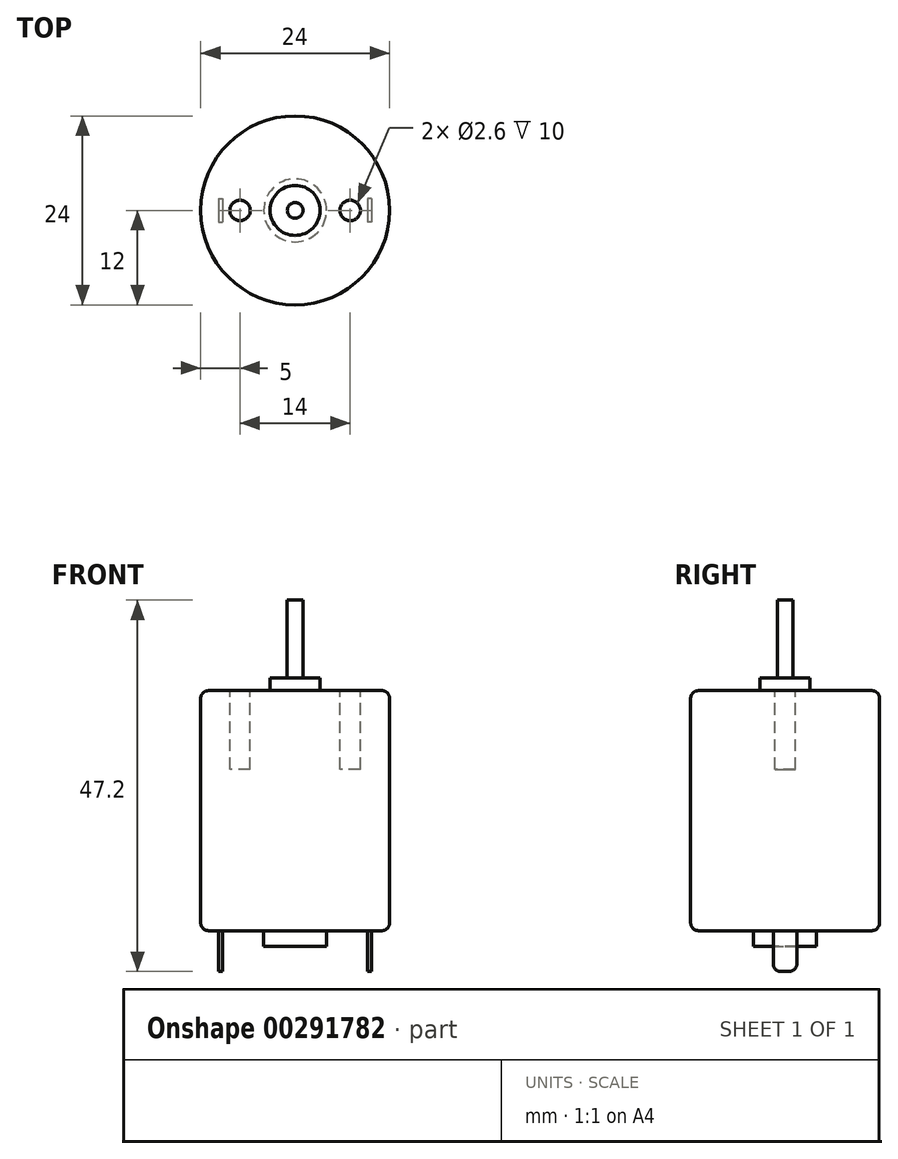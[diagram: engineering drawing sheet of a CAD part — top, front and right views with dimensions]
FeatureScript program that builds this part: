
annotation { "Feature Type Name" : "Feature", "Feature Type Description" : "" }
export const myFeature = defineFeature(function(context is Context, id is Id, definition is map)
    precondition{}
    {
        {
            var Q0;
            Q0=qCreatedBy(makeId("Top.planeOp"),FACE);
            var sketch = newSketch(context, id + "F0", { "sketchPlane" : qUnion([Q0])});
            skCircle(sketch, "E0", {"center": v(0, 0) * mm, "radius": 12 * mm});
            skSolve(sketch);
        }
        {
            var Q0;
            Q0=makeQuery(id+"F0.imprint","IMPRINT",FACE,{"disambiguationData":[TD([[makeQuery(id+"F0.imprint","IMPRINT",EDGE,{"derivedFrom":sQuery(id+"F0.wireOp",EDGE,"E0")}),1.0]])]});
            extrude(context, id + "F1", {"entities" : qUnion([Q0]), "depth" : 30.5 * mm});
        }
        {
            var Q0;
            Q0=makeQuery(id+"F1.opExtrude","CAP_FACE",FACE,{"disambiguationData":[OSD([sQuery(id+"F0.wireOp",EDGE,"E0")])],"isStart":false});
            var sketch = newSketch(context, id + "F2", { "sketchPlane" : qUnion([Q0])});
            skCircle(sketch, "E1", {"center": v(0, 0) * mm, "radius": 1 * mm});
            skSolve(sketch);
        }
        {
            var Q0;
            Q0 = qSketchRegion(id + "F2", true);
            extrude(context, id + "F3", {"entities" : qUnion([Q0]), "operationType" : NewBodyOperationType.ADD, "depth" : 11.5 * mm});
        }
        {
            var Q0;
            Q0=makeQuery(id+"F1.opExtrude","CAP_FACE",FACE,{"disambiguationData":[OSD([sQuery(id+"F0.wireOp",EDGE,"E0")])],"isStart":false});
            var sketch = newSketch(context, id + "F4", { "sketchPlane" : qUnion([Q0])});
            skCircle(sketch, "E2", {"center": v(0, 0) * mm, "radius": 3.17 * mm});
            skSolve(sketch);
        }
        {
            var Q0;
            Q0 = qSketchRegion(id + "F4", true);
            extrude(context, id + "F5", {"entities" : qUnion([Q0]), "operationType" : NewBodyOperationType.ADD, "depth" : 1.6 * mm});
        }
        {
            var Q0;
            Q0=makeQuery(id+"F1.opExtrude","CAP_FACE",FACE,{"disambiguationData":[OSD([sQuery(id+"F0.wireOp",EDGE,"E0")])],"isStart":false});
            var sketch = newSketch(context, id + "F6", { "sketchPlane" : qUnion([Q0])});
            skLineSegment(sketch, "E3", {"start": v(-12, 0) * mm, "end": v(12, 0) * mm, "construction": true});
            skCircle(sketch, "E4", {"center": v(7, 0) * mm, "radius": 1.3 * mm});
            skCircle(sketch, "E5", {"center": v(-7, 0) * mm, "radius": 1.3 * mm});
            skLineSegment(sketch, "E6", {"start": v(0, -12) * mm, "end": v(0, 12) * mm, "construction": true});
            skSolve(sketch);
        }
        {
            var Q0;
            Q0=makeQuery(id+"F6.imprint","IMPRINT",FACE,{"disambiguationData":[TD([[makeQuery(id+"F6.imprint","IMPRINT",EDGE,{"derivedFrom":sQuery(id+"F6.wireOp",EDGE,"E5")}),1.0]])]});
            var Q1;
            Q1=makeQuery(id+"F6.imprint","IMPRINT",FACE,{"disambiguationData":[TD([[makeQuery(id+"F6.imprint","IMPRINT",EDGE,{"derivedFrom":sQuery(id+"F6.wireOp",EDGE,"E4")}),1.0]])]});
            extrude(context, id + "F7", {"entities" : qUnion([Q0, Q1]), "operationType" : NewBodyOperationType.REMOVE, "oppositeDirection" : true, "depth" : 10 * mm});
        }
        {
            var Q0;
            Q0=makeQuery(id+"F1.opExtrude","CAP_FACE",FACE,{"disambiguationData":[OSD([sQuery(id+"F0.wireOp",EDGE,"E0")])],"isStart":true});
            var sketch = newSketch(context, id + "F8", { "sketchPlane" : qUnion([Q0])});
            skCircle(sketch, "E7", {"center": v(0, 0) * mm, "radius": 4 * mm});
            skSolve(sketch);
        }
        {
            var Q0;
            Q0=makeQuery(id+"F8.imprint","IMPRINT",FACE,{"disambiguationData":[TD([[makeQuery(id+"F8.imprint","IMPRINT",EDGE,{"derivedFrom":sQuery(id+"F8.wireOp",EDGE,"E7")}),1.0]])]});
            extrude(context, id + "F9", {"entities" : qUnion([Q0]), "operationType" : NewBodyOperationType.ADD, "depth" : 2 * mm});
        }
        {
            var Q0;
            Q0=makeQuery(id+"F1.opExtrude","CAP_FACE",FACE,{"disambiguationData":[OSD([sQuery(id+"F0.wireOp",EDGE,"E0")])],"isStart":true});
            var sketch = newSketch(context, id + "F10", { "sketchPlane" : qUnion([Q0])});
            skLineSegment(sketch, "E8.bottom", {"start": v(-9.7, -1.5) * mm, "end": v(-9.2, -1.5) * mm});
            skLineSegment(sketch, "E8.top", {"start": v(-9.7, 1.5) * mm, "end": v(-9.2, 1.5) * mm});
            skLineSegment(sketch, "E8.left", {"start": v(-9.7, -1.5) * mm, "end": v(-9.7, 1.5) * mm});
            skLineSegment(sketch, "E8.right", {"start": v(-9.2, -1.5) * mm, "end": v(-9.2, 1.5) * mm});
            skLineSegment(sketch, "E9", {"start": v(0, 12) * mm, "end": v(0, -12) * mm, "construction": true});
            skLineSegment(sketch, "E10", {"start": v(12, 0) * mm, "end": v(-12, 0) * mm, "construction": true});
            skLineSegment(sketch, "E11.bottom", {"start": v(9.7, -1.5) * mm, "end": v(9.2, -1.5) * mm});
            skLineSegment(sketch, "E11.top", {"start": v(9.7, 1.5) * mm, "end": v(9.2, 1.5) * mm});
            skLineSegment(sketch, "E11.left", {"start": v(9.7, -1.5) * mm, "end": v(9.7, 1.5) * mm});
            skLineSegment(sketch, "E11.right", {"start": v(9.2, -1.5) * mm, "end": v(9.2, 1.5) * mm});
            skSolve(sketch);
        }
        {
            var Q0;
            Q0=makeQuery(id+"F10.imprint","IMPRINT",FACE,{"disambiguationData":[TD([[makeQuery(id+"F10.imprint","IMPRINT",EDGE,{"derivedFrom":sQuery(id+"F10.wireOp",EDGE,"E8.bottom")}),1.0]])]});
            var Q1;
            Q1=makeQuery(id+"F10.imprint","IMPRINT",FACE,{"disambiguationData":[TD([[makeQuery(id+"F10.imprint","IMPRINT",EDGE,{"derivedFrom":sQuery(id+"F10.wireOp",EDGE,"E11.bottom")}),-1.0]])]});
            extrude(context, id + "F11", {"entities" : qUnion([Q0, Q1]), "operationType" : NewBodyOperationType.ADD, "depth" : 5.2 * mm});
        }
        {
            var Q0;
            Q0=makeQuery(id+"F11.opExtrude","CAP_EDGE",EDGE,{"disambiguationData":[OSD([sQuery(id+"F10.wireOp",EDGE,"E8.bottom")])],"isStart":false});
            var Q1;
            Q1=makeQuery(id+"F11.opExtrude","CAP_EDGE",EDGE,{"disambiguationData":[OSD([sQuery(id+"F10.wireOp",EDGE,"E8.top")])],"isStart":false});
            var Q2;
            Q2=makeQuery(id+"F11.opExtrude","CAP_EDGE",EDGE,{"disambiguationData":[OSD([sQuery(id+"F10.wireOp",EDGE,"E11.bottom")])],"isStart":false});
            var Q3;
            Q3=makeQuery(id+"F11.opExtrude","CAP_EDGE",EDGE,{"disambiguationData":[OSD([sQuery(id+"F10.wireOp",EDGE,"E11.top")])],"isStart":false});
            fillet(context, id + "F12", {"entities" : qUnion([Q0, Q1, Q2, Q3]), "radius" : 1 * mm, "tangentPropagation" : true, "allowEdgeOverflow" : false});
        }
        {
            var Q0;
            Q0=makeQuery(id+"F1.opExtrude","CAP_EDGE",EDGE,{"disambiguationData":[OSD([sQuery(id+"F0.wireOp",EDGE,"E0")])],"isStart":true});
            fillet(context, id + "F13", {"entities" : qUnion([Q0]), "radius" : 1 * mm, "tangentPropagation" : true, "allowEdgeOverflow" : false});
        }
        {
            var Q0;
            Q0=makeQuery(id+"F1.opExtrude","CAP_EDGE",EDGE,{"disambiguationData":[OSD([sQuery(id+"F0.wireOp",EDGE,"E0")])],"isStart":false});
            fillet(context, id + "F14", {"entities" : qUnion([Q0]), "radius" : 1 * mm, "tangentPropagation" : true, "allowEdgeOverflow" : false});
        }
    });
